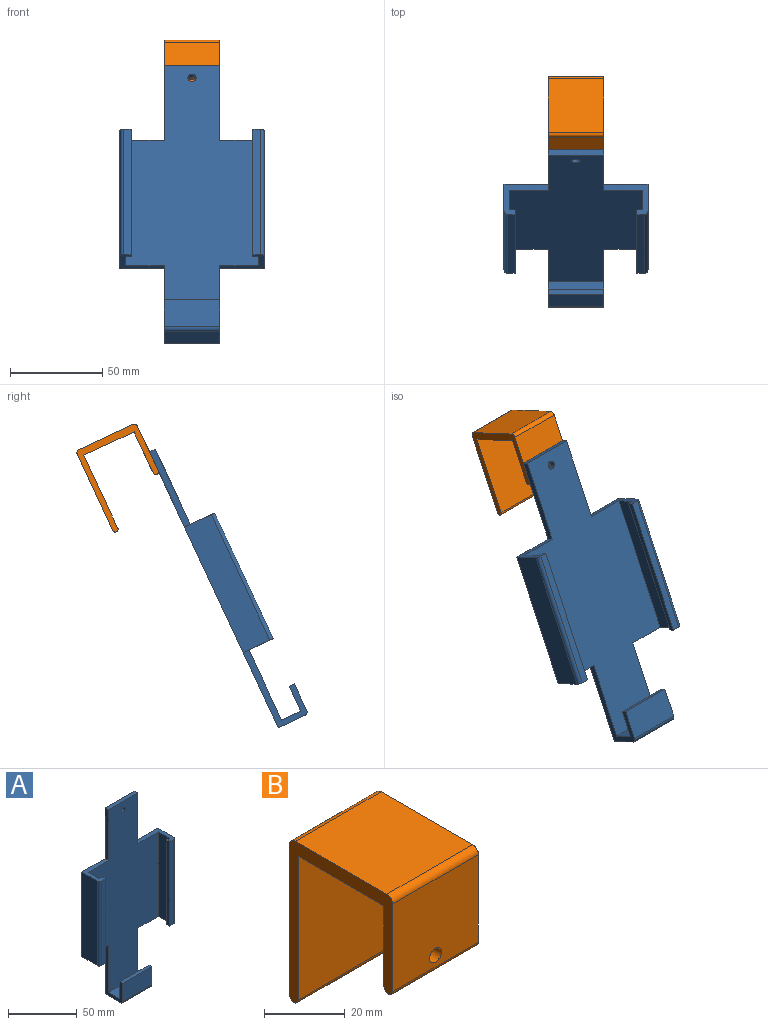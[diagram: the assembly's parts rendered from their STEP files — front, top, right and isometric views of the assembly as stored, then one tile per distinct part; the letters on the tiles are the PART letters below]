
ASSEMBLY  parts=2 mates=1
PART A: 30 faces, bbox 78x18x165 mm
  f0: plane 75x11.5mm, normal (-1,0,0), area 862.5mm2, adj f2,f12,f14,f24
  f1: plane 75x11.5mm, normal (1,0,0), area 862.5mm2, adj f2,f6,f8,f22
  f2: plane 162x72mm, normal (0,-1,0), area 7994.8mm2, adj f0,f1,f3,f4,f5,f6,f8,f9
  f3: plane 45x3.5mm, normal (1,0,0), area 157.5mm2, adj f2,f4,f14,f15
  f4: plane 30x3.5mm, normal (0,0,1), area 105mm2, adj f2,f3,f5,f15
  f5: plane 45x3.5mm, normal (-1,0,0), area 157.5mm2, adj f2,f4,f6,f15
  f6: plane 24x18mm, normal (0,0,1), area 135.6mm2, adj f1,f2,f5,f7,f15,f20,f22,f23
  f7: plane 75x16mm, normal (-1,0,0), area 1200mm2, adj f6,f8,f15,f27
  f8: plane 24x18mm, normal (0,0,-1), area 135.6mm2, adj f1,f2,f7,f9,f15,f20,f22,f23
  f9: plane 45x18mm, normal (-1,0,0), area 245.1mm2, adj f2,f8,f10,f15,f16,f17,f18,f19
  f10: plane 30x16mm, normal (0,0,-1), area 480mm2, adj f9,f11,f15,f28
  f11: plane 45x18mm, normal (1,0,0), area 245.1mm2, adj f2,f10,f12,f15,f16,f17,f18,f19
  f12: plane 24x18mm, normal (0,0,-1), area 135.6mm2, adj f0,f2,f11,f13,f15,f21,f24,f25
  f13: plane 75x16mm, normal (1,0,0), area 1200mm2, adj f12,f14,f15,f26
  f14: plane 24x18mm, normal (0,0,1), area 135.6mm2, adj f0,f2,f3,f13,f15,f21,f24,f25
  f15: plane 165x78mm, normal (0,1,0), area 8534.8mm2, adj f3,f4,f5,f6,f7,f8,f9,f10
  f16: plane 30x11.5mm, normal (0,0,1), area 345mm2, adj f2,f9,f11,f18
  f17: plane 30x16mm, normal (0,-1,0), area 480mm2, adj f9,f11,f19,f28
  f18: plane 30x15mm, normal (0,1,0), area 450mm2, adj f9,f11,f16,f19
  f19: plane 30x3mm, normal (0,0,1), area 90mm2, adj f9,f11,f17,f18
  f20: plane 75x4mm, normal (0,-1,0), area 300mm2, adj f6,f8,f23,f27
  f21: plane 75x4mm, normal (0,-1,0), area 300mm2, adj f12,f14,f25,f26
  f22: plane 75x3mm, normal (0,1,0), area 225mm2, adj f1,f6,f8,f23
  f23: plane 75x3mm, normal (1,0,0), area 225mm2, adj f6,f8,f20,f22
  f24: plane 75x3mm, normal (0,1,0), area 225mm2, adj f0,f12,f14,f25
  f25: plane 75x3mm, normal (-1,0,0), area 225mm2, adj f12,f14,f21,f24
  f26: cylinder r=2mm len=75mm, axis (0,0,-1), area 235.6mm2, adj f12,f13,f14,f21
  f27: cylinder r=2mm len=75mm, axis (0,0,1), area 235.6mm2, adj f6,f7,f8,f20
  f28: cylinder r=2mm len=30mm, axis (-1,0,0), area 94.2mm2, adj f9,f10,f11,f17
  f29: cylinder r=2.2mm len=4.4mm, axis (0,-1,0), area 48.4mm2, adj f2,f15
PART B: 13 faces, bbox 30x36x49 mm
  f0: plane 30x24.5mm, normal (0,1,0), area 721.1mm2, adj f1,f2,f5,f8,f9
  f1: plane 49x36mm, normal (-1,0,0), area 353.4mm2, adj f0,f3,f4,f5,f6,f7,f9,f10
  f2: plane 49x36mm, normal (1,0,0), area 353.4mm2, adj f0,f3,f4,f5,f6,f7,f9,f10
  f3: plane 32x30mm, normal (0,0,1), area 960mm2, adj f1,f2,f7,f12
  f4: plane 30x26.5mm, normal (0,-1,0), area 781.1mm2, adj f1,f2,f7,f8,f9
  f5: plane 30x30mm, normal (0,0,-1), area 900mm2, adj f0,f1,f2,f10
  f6: plane 45.5x30mm, normal (0,1,0), area 1365mm2, adj f1,f2,f11,f12
  f7: cylinder r=2mm len=30mm, axis (1,0,0), area 94.2mm2, adj f1,f2,f3,f4
  f8: cylinder r=2.1mm len=4.2mm, axis (0,-1,0), area 39.6mm2, adj f0,f4
  f9: cylinder r=1.5mm len=30mm, axis (-1,0,0), area 141.4mm2, adj f0,f1,f2,f4
  f10: plane 43.5x30mm, normal (0,-1,0), area 1305mm2, adj f1,f2,f5,f11
  f11: cylinder r=1.5mm len=30mm, axis (1,0,0), area 141.4mm2, adj f1,f2,f6,f10
  f12: cylinder r=2mm len=30mm, axis (1,0,0), area 94.2mm2, adj f1,f2,f3,f6
PLACE A rot(axis=(-1,0,0),25deg) t=(-20,-45.85,38.74)mm
PLACE B rot(axis=(-1,0,0),25deg) t=(-22.12,-18.49,90.31)mm
MATE revolute A.f29 <-> B.f8  axis (0,0.91,-0.42) through (-20,-14.24,106.53)mm
